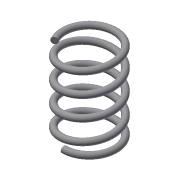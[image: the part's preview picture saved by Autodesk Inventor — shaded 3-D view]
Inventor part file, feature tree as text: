
AUTODESK INVENTOR PART (.ipt)
format: ipt  version: 2016 (Build 200138000, 138)  size: 347,648 bytes
history: native  units: mm
features: helix x1
ambient origin geometry x8: Origin, YZ Plane, XZ Plane, XY Plane, X Axis, Y Axis, Z Axis, Center Point
bodies: Body1 (feature_tree)
feature tree (1):
  helix  "Coil2"  [1 undecoded]
note: 1 required parameter value undecoded (feature->parameter linkage not recoverable at this tier; creation-order binding heuristic only, values carry confidence <= 0.55)
